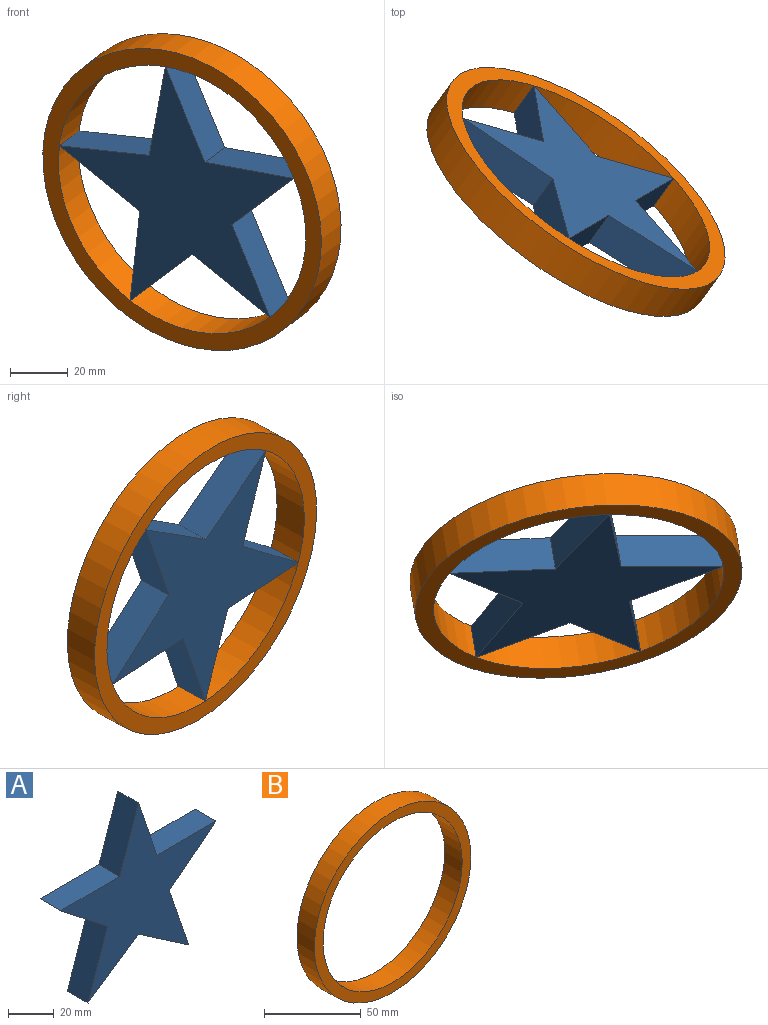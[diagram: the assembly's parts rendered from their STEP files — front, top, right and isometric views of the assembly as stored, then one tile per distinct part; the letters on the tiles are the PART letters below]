
ASSEMBLY  parts=2 mates=1
PART A: 12 faces, bbox 95.5x12.7x91.1 mm
  f0: plane 36.26x12.7mm, normal (0,0,1), area 460.5mm2, adj f1,f9,f10,f11
  f1: plane 33.5x12.7mm, normal (0.95,0,0.32), area 449.8mm2, adj f0,f2,f10,f11
  f2: plane 33.5x12.7mm, normal (-0.95,0,0.32), area 449.8mm2, adj f1,f3,f10,f11
  f3: plane 36.26x12.7mm, normal (0,0,1), area 460.5mm2, adj f2,f4,f10,f11
  f4: plane 28.76x22.87mm, normal (-0.62,0,-0.78), area 466.7mm2, adj f3,f5,f10,f11
  f5: plane 34.73x12.7mm, normal (-0.95,0,0.32), area 466.3mm2, adj f4,f6,f10,f11
  f6: plane 30.93x21.23mm, normal (0.57,0,-0.82), area 476.4mm2, adj f5,f7,f10,f11
  f7: plane 30.93x21.23mm, normal (-0.57,0,-0.82), area 476.4mm2, adj f6,f8,f10,f11
  f8: plane 34.73x12.7mm, normal (0.95,0,0.32), area 466.3mm2, adj f7,f9,f10,f11
  f9: plane 28.76x22.87mm, normal (0.62,0,-0.78), area 466.7mm2, adj f0,f8,f10,f11
  f10: plane 95.53x91.1mm, normal (0,-1,0), area 2989.7mm2, adj f0,f1,f2,f3,f4,f5,f6,f7
  f11: plane 95.53x91.1mm, normal (0,1,0), area 2989.7mm2, adj f0,f1,f2,f3,f4,f5,f6,f7
PART B: 4 faces, bbox 114.3x12.7x114.3 mm
  f0: cylinder r=50.8mm len=101.6mm, axis (0,1,0), area 4053.7mm2, adj f2,f3
  f1: cylinder r=57.15mm len=114.3mm, axis (0,1,0), area 4560.4mm2, adj f2,f3
  f2: plane 114.3x114.3mm, normal (0,-1,0), area 2153.5mm2, adj f0,f1
  f3: plane 114.3x114.3mm, normal (0,1,0), area 2153.5mm2, adj f0,f1
PLACE A rot(axis=(-0.89,0.34,-0.3),166.8deg) t=(938.58,-797.55,2265.03)mm
PLACE B rot(axis=(0.42,-0.33,0.84),161.5deg) t=(938.58,-797.55,2265.03)mm
MATE planar A.f11 <-> B.f0  axis (-0.54,-0.74,-0.4) through (939,-797.55,2264.47)mm
